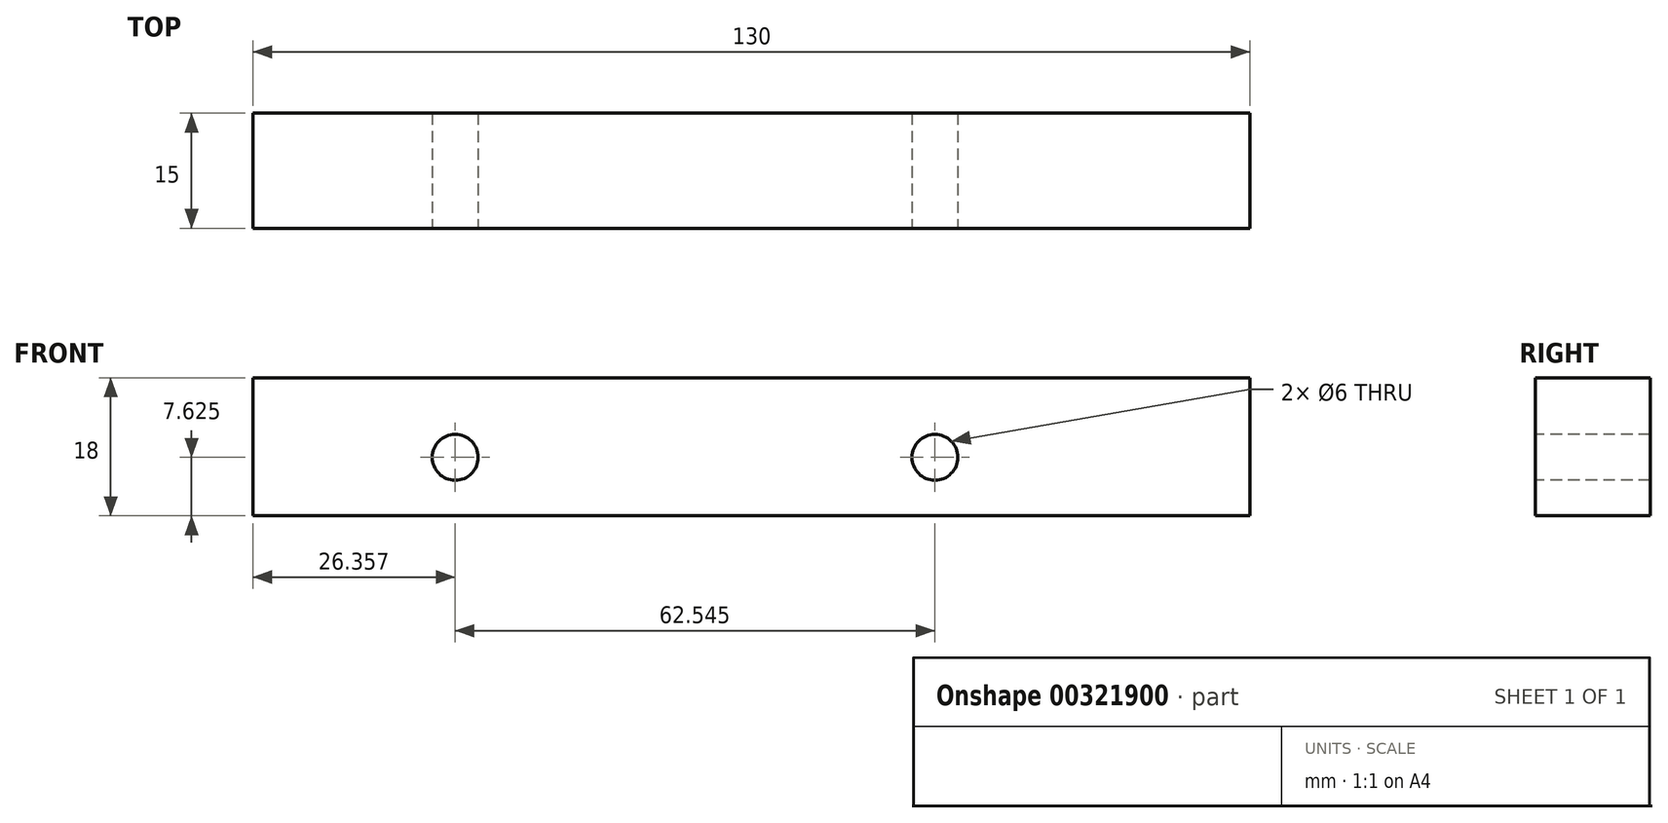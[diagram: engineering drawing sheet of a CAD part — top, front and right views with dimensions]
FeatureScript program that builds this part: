
annotation { "Feature Type Name" : "Feature", "Feature Type Description" : "" }
export const myFeature = defineFeature(function(context is Context, id is Id, definition is map)
    precondition{}
    {
        {
            var Q0;
            Q0=qCreatedBy(makeId("Front.planeOp"),FACE);
            var sketch = newSketch(context, id + "F0", { "sketchPlane" : qUnion([Q0])});
            skLineSegment(sketch, "E0.bottom", {"start": v(-65, 0) * mm, "end": v(65, 0) * mm});
            skLineSegment(sketch, "E0.top", {"start": v(-65, -18) * mm, "end": v(65, -18) * mm});
            skLineSegment(sketch, "E0.left", {"start": v(-65, 0) * mm, "end": v(-65, -18) * mm});
            skLineSegment(sketch, "E0.right", {"start": v(65, 0) * mm, "end": v(65, -18) * mm});
            skCircle(sketch, "E1", {"center": v(-32.95, -9.84) * mm, "radius": 3 * mm});
            skCircle(sketch, "E2", {"center": v(41.16, -9.84) * mm, "radius": 3 * mm});
            skSolve(sketch);
        }
        {
            var Q0;
            Q0=makeQuery(id+"F0.imprint","IMPRINT",FACE,{"disambiguationData":[TD([[makeQuery(id+"F0.imprint","IMPRINT",EDGE,{"derivedFrom":sQuery(id+"F0.wireOp",EDGE,"E0.bottom")}),-1.0]])]});
            var Q1;
            Q1=makeQuery(id+"F0.imprint","IMPRINT",FACE,{"disambiguationData":[TD([[makeQuery(id+"F0.imprint","IMPRINT",EDGE,{"derivedFrom":sQuery(id+"F0.wireOp",EDGE,"E1")}),1.0]])]});
            var Q2;
            Q2=makeQuery(id+"F0.imprint","IMPRINT",FACE,{"disambiguationData":[TD([[makeQuery(id+"F0.imprint","IMPRINT",EDGE,{"derivedFrom":sQuery(id+"F0.wireOp",EDGE,"E2")}),1.0]])]});
            extrude(context, id + "F1", {"entities" : qUnion([Q0, Q1, Q2]), "endBound" : BoundingType.SYMMETRIC, "depth" : 15 * mm});
        }
        {
            var Q0;
            Q0=qCreatedBy(makeId("Front.planeOp"),FACE);
            var sketch = newSketch(context, id + "F2", { "sketchPlane" : qUnion([Q0])});
            skCircle(sketch, "E3", {"center": v(-38.64, -10.37) * mm, "radius": 3 * mm});
            skCircle(sketch, "E4", {"center": v(23.9, -10.37) * mm, "radius": 3 * mm});
            skSolve(sketch);
        }
        {
            var Q0;
            Q0 = qSketchRegion(id + "F2", true);
            extrude(context, id + "F3", {"entities" : qUnion([Q0]), "operationType" : NewBodyOperationType.REMOVE, "endBound" : BoundingType.THROUGH_ALL, "oppositeDirection" : true, "depth" : 25 * mm, "hasSecondDirection" : true, "secondDirectionOppositeDirection" : false, "secondDirectionDepth" : 25 * mm});
        }
    });
